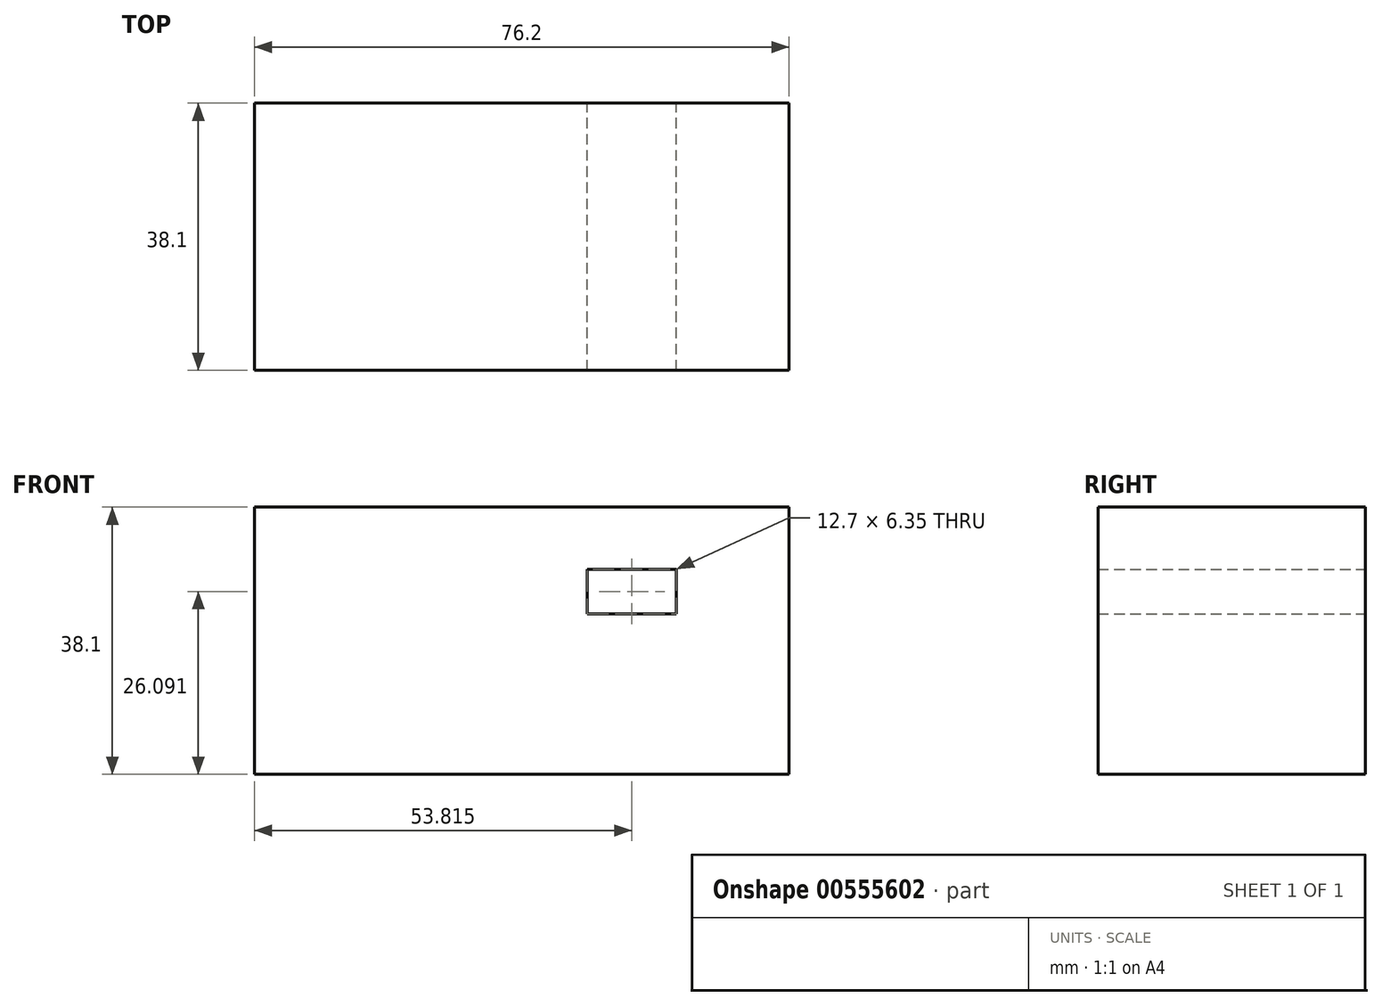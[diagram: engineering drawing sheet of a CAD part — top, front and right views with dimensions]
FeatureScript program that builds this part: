
annotation { "Feature Type Name" : "Feature", "Feature Type Description" : "" }
export const myFeature = defineFeature(function(context is Context, id is Id, definition is map)
    precondition{}
    {
        {
            var Q0;
            Q0=qCreatedBy(makeId("Front.planeOp"),FACE);
            var sketch = newSketch(context, id + "F0", { "sketchPlane" : qUnion([Q0])});
            skLineSegment(sketch, "E0.bottom", {"start": v(-38.1, 19.05) * mm, "end": v(38.1, 19.05) * mm});
            skLineSegment(sketch, "E0.top", {"start": v(-38.1, -19.05) * mm, "end": v(38.1, -19.05) * mm});
            skLineSegment(sketch, "E0.left", {"start": v(-38.1, 19.05) * mm, "end": v(-38.1, -19.05) * mm});
            skLineSegment(sketch, "E0.right", {"start": v(38.1, 19.05) * mm, "end": v(38.1, -19.05) * mm});
            skPoint(sketch, "E0.middle", {"position": v(0, 0) * mm});
            skLineSegment(sketch, "E1.bottom", {"start": v(22.06, 3.87) * mm, "end": v(9.36, 3.87) * mm});
            skLineSegment(sketch, "E1.top", {"start": v(22.06, 10.22) * mm, "end": v(9.36, 10.22) * mm});
            skLineSegment(sketch, "E1.left", {"start": v(22.06, 3.87) * mm, "end": v(22.06, 10.22) * mm});
            skLineSegment(sketch, "E1.right", {"start": v(9.36, 3.87) * mm, "end": v(9.36, 10.22) * mm});
            skPoint(sketch, "E1.middle", {"position": v(15.71, 7.04) * mm});
            skSolve(sketch);
        }
        {
            var Q0;
            Q0 = qSketchRegion(id + "F0", true);
            extrude(context, id + "F1", {"entities" : qUnion([Q0]), "depth" : 38.1 * mm, "offsetDistance" : 25.4 * mm});
        }
    });
